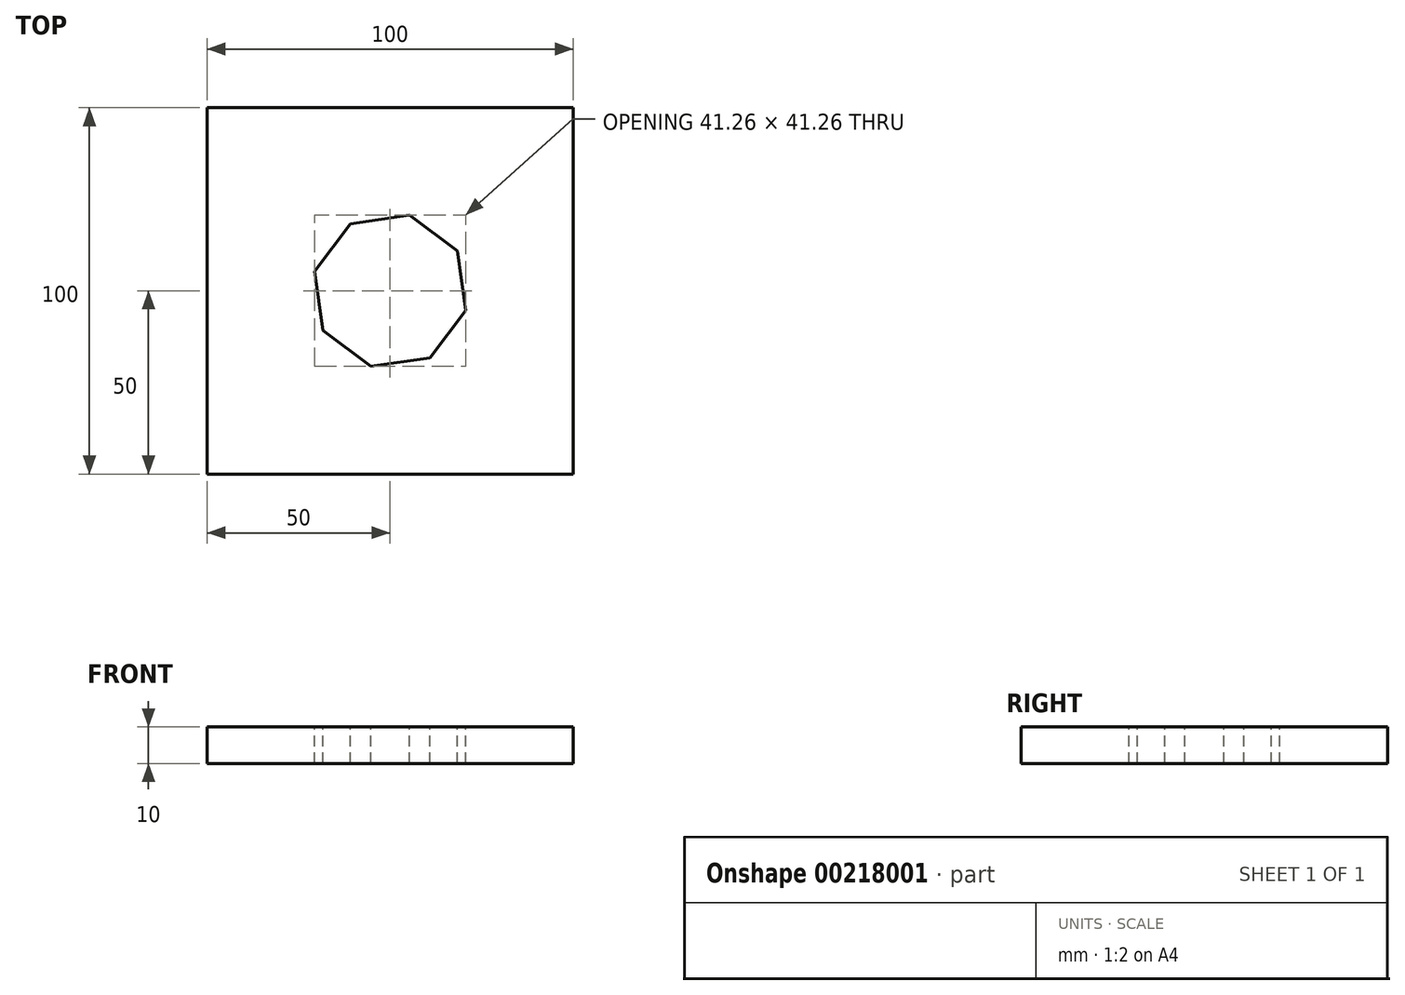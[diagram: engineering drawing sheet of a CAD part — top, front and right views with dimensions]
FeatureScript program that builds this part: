
annotation { "Feature Type Name" : "Feature", "Feature Type Description" : "" }
export const myFeature = defineFeature(function(context is Context, id is Id, definition is map)
    precondition{}
    {
        {
            var Q0;
            Q0=qCreatedBy(makeId("Top.planeOp"),FACE);
            var sketch = newSketch(context, id + "F0", { "sketchPlane" : qUnion([Q0])});
            skLineSegment(sketch, "E0.bottom", {"start": v(50, -50) * mm, "end": v(-50, -50) * mm});
            skLineSegment(sketch, "E0.top", {"start": v(50, 50) * mm, "end": v(-50, 50) * mm});
            skLineSegment(sketch, "E0.left", {"start": v(50, -50) * mm, "end": v(50, 50) * mm});
            skLineSegment(sketch, "E0.right", {"start": v(-50, -50) * mm, "end": v(-50, 50) * mm});
            skPoint(sketch, "E0.middle", {"position": v(0, 0) * mm});
            skSolve(sketch);
        }
        {
            var Q0;
            Q0 = qSketchRegion(id + "FvlIdyHgMXoRbfs_0", true);
            var Q1;
            Q1=makeQuery(id+"F0.imprint","IMPRINT",FACE,{"disambiguationData":[TD([[makeQuery(id+"F0.imprint","IMPRINT",EDGE,{"derivedFrom":sQuery(id+"F0.wireOp",EDGE,"E0.bottom")}),-1.0]])]});
            extrude(context, id + "F1", {"entities" : qUnion([Q0, Q1]), "oppositeDirection" : true, "depth" : 10 * mm});
        }
        {
            var Q0;
            Q0=makeQuery(id+"F1.opExtrude","CAP_FACE",FACE,{"disambiguationData":[OSD([sQuery(id+"F0.wireOp",EDGE,"E0.bottom"),sQuery(id+"F0.wireOp",EDGE,"E0.top"),sQuery(id+"F0.wireOp",EDGE,"E0.left"),sQuery(id+"F0.wireOp",EDGE,"E0.right")])],"isStart":true});
            var sketch = newSketch(context, id + "F2", { "sketchPlane" : qUnion([Q0])});
            skCircle(sketch, "E1.cCircle", {"center": v(0, 0) * mm, "radius": 19.67 * mm, "construction": true});
            skLineSegment(sketch, "E1.0", {"start": v(20.63, -5.29) * mm, "end": v(10.85, -18.32) * mm});
            skLineSegment(sketch, "E1.1", {"start": v(10.85, -18.32) * mm, "end": v(-5.29, -20.63) * mm});
            skLineSegment(sketch, "E1.2", {"start": v(-5.29, -20.63) * mm, "end": v(-18.32, -10.85) * mm});
            skLineSegment(sketch, "E1.3", {"start": v(-18.32, -10.85) * mm, "end": v(-20.63, 5.29) * mm});
            skLineSegment(sketch, "E1.4", {"start": v(-20.63, 5.29) * mm, "end": v(-10.85, 18.32) * mm});
            skLineSegment(sketch, "E1.5", {"start": v(-10.85, 18.32) * mm, "end": v(5.29, 20.63) * mm});
            skLineSegment(sketch, "E1.6", {"start": v(5.29, 20.63) * mm, "end": v(18.32, 10.85) * mm});
            skLineSegment(sketch, "E1.7", {"start": v(18.32, 10.85) * mm, "end": v(20.63, -5.29) * mm});
            skPoint(sketch, "E1.0.midPoint", {"position": v(15.74, -11.8) * mm});
            skSolve(sketch);
        }
        {
            var Q0;
            Q0=makeQuery(id+"F2.imprint","IMPRINT",FACE,{"disambiguationData":[TD([[makeQuery(id+"F2.imprint","IMPRINT",EDGE,{"derivedFrom":sQuery(id+"F2.wireOp",EDGE,"E1.0")}),-1.0]])]});
            extrude(context, id + "F3", {"entities" : qUnion([Q0]), "operationType" : NewBodyOperationType.REMOVE, "oppositeDirection" : true, "depth" : 39.62 * mm});
        }
    });
